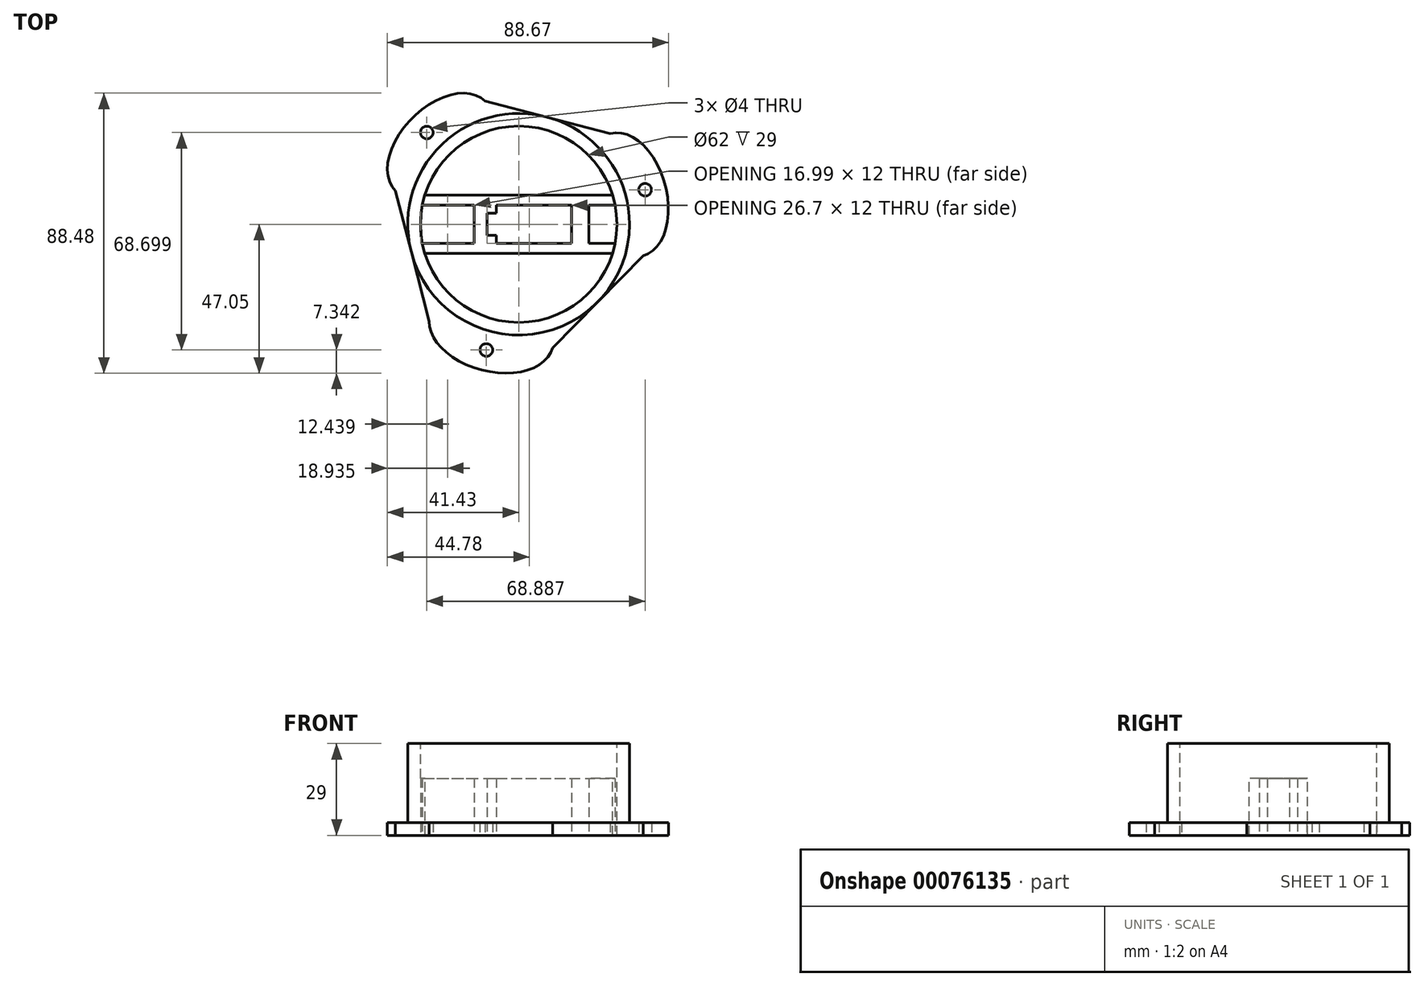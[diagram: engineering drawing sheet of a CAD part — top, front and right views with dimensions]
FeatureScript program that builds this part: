
annotation { "Feature Type Name" : "Feature", "Feature Type Description" : "" }
export const myFeature = defineFeature(function(context is Context, id is Id, definition is map)
    precondition{}
    {
        {
            var Q0;
            Q0=qCreatedBy(makeId("Top.planeOp"),FACE);
            var sketch = newSketch(context, id + "F0", { "sketchPlane" : qUnion([Q0])});
            skCircle(sketch, "E0", {"center": v(0, 0) * mm, "radius": 35 * mm, "construction": true});
            skLineSegment(sketch, "E1", {"start": v(0, 0) * mm, "end": v(-53.68, 53.68) * mm, "construction": true});
            skLineSegment(sketch, "E2", {"start": v(-24.75, 24.75) * mm, "end": v(-10.6, 38.9) * mm, "construction": true});
            skPoint(sketch, "E2.endSnap0", {"position": v(-10.6, 38.9) * mm});
            skPoint(sketch, "E3.center", {"position": v(0.23, 0.06) * mm});
            skLineSegment(sketch, "E4", {"start": v(-10.6, 38.9) * mm, "end": v(28.92, 28.68) * mm});
            skLineSegment(sketch, "E5", {"start": v(39.28, -9.96) * mm, "end": v(10.66, -39.09) * mm});
            skLineSegment(sketch, "E6", {"start": v(-38.9, 10.6) * mm, "end": v(-28.24, -30.6) * mm});
            skLineSegment(sketch, "E7", {"start": v(10.66, -39.09) * mm, "end": v(-8.65, -33.91) * mm, "construction": true});
            skEllipticalArc(sketch, "E8", {});
            skEllipticalArc(sketch, "E9", {"construction": true});
            skEllipticalArc(sketch, "E10", {"construction": true});
            skEllipticalArc(sketch, "E11", {});
            skEllipticalArc(sketch, "E12", {});
            skEllipticalArc(sketch, "E13", {"construction": true});
            skCircle(sketch, "E14", {"center": v(-29, 29) * mm, "radius": 2 * mm});
            skCircle(sketch, "E15.1.0", {"center": v(-10.2, -39.7) * mm, "radius": 2 * mm});
            skCircle(sketch, "E15.2.0", {"center": v(39.9, 10.9) * mm, "radius": 2 * mm});
            const initialGuessF0  = {"E8": [-0.024748737341529166, 0.024748737341529166, 0.7071067811865477, 0.7071067811865475, 0.02, 0.0125, 0, 3.141592653589793], "E9": [-0.024748737341529173, 0.02474873734152916, 0.7071067811865474, 0.7071067811865478, 0.02, 0.0125, 3.141592653589793, 0], "E10": [0.034100125777446366, 0.009356648892922962, 0.258819045102522, -0.965925826289068, 0.02, 0.0125, 3.141592653589793, 0], "E11": [0.034100125777446366, 0.009356648892922962, 0.25881904510252196, -0.965925826289068, 0.02, 0.0125, 0, 3.141592653589793], "E12": [-0.00865424539583139, -0.03391191732763989, -0.9659258262890683, 0.25881904510252074, 0.02, 0.0125, 0.15088942989360254, 3.141592653589793], "E13": [-0.00865424539583139, -0.03391191732763989, -0.9659258262890683, 0.25881904510252074, 0.02, 0.0125, 3.141592653589793, 0.15088942989360254]};
            skSetInitialGuess(sketch, initialGuessF0);
            skSolve(sketch);
        }
        {
            var Q0;
            Q0=makeQuery(id+"F0.imprint","IMPRINT",FACE,{"disambiguationData":[TD([[makeQuery(id+"F0.imprint","IMPRINT",EDGE,{"derivedFrom":sQuery(id+"F0.wireOp",EDGE,"E4")}),-1.0]])]});
            var Q1;
            Q1=sQuery(id+"F0.wireOp",EDGE,"E4");
            var Q2;
            Q2=sQuery(id+"F0.wireOp",EDGE,"E8");
            var Q3;
            Q3=sQuery(id+"F0.wireOp",EDGE,"E6");
            var Q4;
            Q4=sQuery(id+"F0.wireOp",EDGE,"E12");
            var Q5;
            Q5=sQuery(id+"F0.wireOp",EDGE,"E5");
            var Q6;
            Q6=sQuery(id+"F0.wireOp",EDGE,"E11");
            extrude(context, id + "F1", {"entities" : qUnion([Q0]), "surfaceEntities" : qUnion([Q1, Q2, Q3, Q4, Q5, Q6]), "depth" : 4 * mm});
        }
        {
            var Q0;
            Q0=makeQuery(id+"F1.opExtrude","CAP_FACE",FACE,{"disambiguationData":[OSD([sQuery(id+"F0.wireOp",EDGE,"E4"),sQuery(id+"F0.wireOp",EDGE,"E5"),sQuery(id+"F0.wireOp",EDGE,"E6"),sQuery(id+"F0.wireOp",EDGE,"E8"),sQuery(id+"F0.wireOp",EDGE,"E11"),sQuery(id+"F0.wireOp",EDGE,"E12")])],"isStart":false});
            var sketch = newSketch(context, id + "F2", { "sketchPlane" : qUnion([Q0])});
            skCircle(sketch, "E16", {"center": v(0, 0) * mm, "radius": 35 * mm});
            skSolve(sketch);
        }
        {
            var Q0;
            Q0 = qSketchRegion(id + "F2", true);
            extrude(context, id + "F3", {"entities" : qUnion([Q0]), "operationType" : NewBodyOperationType.ADD, "depth" : 25 * mm});
        }
        {
            var Q0;
            Q0=makeQuery(id+"F3.opExtrude","CAP_FACE",FACE,{"disambiguationData":[OSD([sQuery(id+"F2.wireOp",EDGE,"E16")])],"isStart":false});
            var sketch = newSketch(context, id + "F4", { "sketchPlane" : qUnion([Q0])});
            skCircle(sketch, "E17", {"center": v(0, 0) * mm, "radius": 31 * mm});
            skSolve(sketch);
        }
        {
            var Q0;
            Q0=makeQuery(id+"F4.imprint","IMPRINT",FACE,{"disambiguationData":[TD([[makeQuery(id+"F4.imprint","IMPRINT",EDGE,{"derivedFrom":sQuery(id+"F4.wireOp",EDGE,"E17")}),1.0]])]});
            extrude(context, id + "F5", {"entities" : qUnion([Q0]), "operationType" : NewBodyOperationType.REMOVE, "endBound" : BoundingType.THROUGH_ALL, "oppositeDirection" : true, "depth" : 25 * mm});
        }
        {
            var Q0;
            Q0=qCreatedBy(makeId("Top.planeOp"),FACE);
            var sketch = newSketch(context, id + "F6", { "sketchPlane" : qUnion([Q0])});
            skLineSegment(sketch, "E18.bottom", {"start": v(-31.5, 9.25) * mm, "end": v(31.5, 9.25) * mm});
            skLineSegment(sketch, "E18.top", {"start": v(-31.5, -9.25) * mm, "end": v(31.5, -9.25) * mm});
            skLineSegment(sketch, "E18.left", {"start": v(-31.5, 9.25) * mm, "end": v(-31.5, -9.25) * mm});
            skLineSegment(sketch, "E18.right", {"start": v(31.5, 9.25) * mm, "end": v(31.5, -9.25) * mm});
            skPoint(sketch, "E18.middle", {"position": v(0, 0) * mm});
            skSolve(sketch);
        }
        {
            var Q0;
            Q0=makeQuery(id+"F6.imprint","IMPRINT",FACE,{"disambiguationData":[TD([[makeQuery(id+"F6.imprint","IMPRINT",EDGE,{"derivedFrom":sQuery(id+"F6.wireOp",EDGE,"E18.bottom")}),-1.0]])]});
            extrude(context, id + "F7", {"entities" : qUnion([Q0]), "operationType" : NewBodyOperationType.ADD, "depth" : 18 * mm});
        }
        {
            var Q0;
            Q0=qCreatedBy(makeId("Top.planeOp"),FACE);
            var sketch = newSketch(context, id + "F8", { "sketchPlane" : qUnion([Q0])});
            skLineSegment(sketch, "E19.bottom", {"start": v(31.5, 9.25) * mm, "end": v(-31.5, 9.25) * mm});
            skLineSegment(sketch, "E19.top", {"start": v(31.5, -9.25) * mm, "end": v(-31.5, -9.25) * mm});
            skLineSegment(sketch, "E19.left", {"start": v(31.5, 9.25) * mm, "end": v(31.5, -9.25) * mm, "construction": true});
            skLineSegment(sketch, "E19.right", {"start": v(-31.5, 9.25) * mm, "end": v(-31.5, -9.25) * mm, "construction": true});
            skPoint(sketch, "E19.middle", {"position": v(0, 0) * mm});
            skLineSegment(sketch, "E20.bottom", {"start": v(-14, 6) * mm, "end": v(-30.4, 6) * mm});
            skLineSegment(sketch, "E20.top", {"start": v(-14, -6) * mm, "end": v(-32, -6) * mm});
            skLineSegment(sketch, "E20.left", {"start": v(-14, 6) * mm, "end": v(-14, -6) * mm});
            skPoint(sketch, "E20.middle", {"position": v(-23, 0) * mm});
            skLineSegment(sketch, "E21.bottom", {"start": v(16.7, 6) * mm, "end": v(-7, 6) * mm});
            skLineSegment(sketch, "E21.top", {"start": v(16.7, -6) * mm, "end": v(-7, -6) * mm});
            skLineSegment(sketch, "E21.left", {"start": v(16.7, 6) * mm, "end": v(16.7, -6) * mm});
            skLineSegment(sketch, "E21.right", {"start": v(-7, 6) * mm, "end": v(-7, 3.5) * mm});
            skPoint(sketch, "E21.middle", {"position": v(4.85, 0) * mm});
            skLineSegment(sketch, "E22.bottom", {"start": v(-7, 3.5) * mm, "end": v(-10, 3.5) * mm});
            skLineSegment(sketch, "E22.top", {"start": v(-7, -3.5) * mm, "end": v(-10, -3.5) * mm});
            skLineSegment(sketch, "E22.left", {"start": v(-7, 3.5) * mm, "end": v(-7, -3.5) * mm, "construction": true});
            skLineSegment(sketch, "E22.right", {"start": v(-10, 3.5) * mm, "end": v(-10, -3.5) * mm});
            skPoint(sketch, "E22.middle", {"position": v(-8.5, 0) * mm});
            skPoint(sketch, "E22.middle.positionSnap0", {"position": v(-7, 0) * mm});
            skPoint(sketch, "E22.centerSnap0", {"position": v(-7, 0) * mm});
            skLineSegment(sketch, "E23", {"start": v(-7, -3.5) * mm, "end": v(-7, -6) * mm});
            skLineSegment(sketch, "E24.bottom", {"start": v(22.2, 6) * mm, "end": v(30.41, 6) * mm});
            skLineSegment(sketch, "E24.top", {"start": v(22.2, -6) * mm, "end": v(32.33, -6) * mm});
            skLineSegment(sketch, "E24.left", {"start": v(22.2, 6) * mm, "end": v(22.2, -6) * mm});
            skLineSegment(sketch, "E24.right", {"start": v(32.33, 6) * mm, "end": v(32.33, -6) * mm, "construction": true});
            skPoint(sketch, "E24.middle", {"position": v(27.27, 0) * mm});
            skLineSegment(sketch, "E25", {"start": v(30.41, 6) * mm, "end": v(32.33, 6) * mm, "construction": true});
            skArc(sketch, "E26", {"start": v(30.41, -6) * mm, "mid": v(31, 0) * mm, "end": v(30.41, 6) * mm});
            skLineSegment(sketch, "E27", {"start": v(-31.5, 6) * mm, "end": v(-32, 6) * mm});
            skArc(sketch, "E28", {"start": v(-30.41, -6) * mm, "mid": v(-30.04, -7.64) * mm, "end": v(-29.59, -9.25) * mm});
            skArc(sketch, "E29", {"start": v(-30.4, 6) * mm, "mid": v(-31, 0) * mm, "end": v(-30.41, -6) * mm});
            skArc(sketch, "E30.trimOffspring", {"start": v(-29.59, 9.25) * mm, "mid": v(-30.03, 7.64) * mm, "end": v(-30.4, 6) * mm});
            skArc(sketch, "E31.trimOffspring", {"start": v(29.59, -9.25) * mm, "mid": v(30.04, -7.64) * mm, "end": v(30.41, -6) * mm});
            skSolve(sketch);
        }
        {
            var Q0;
            Q0 = qSketchRegion(id + "F8", true);
            extrude(context, id + "F9", {"entities" : qUnion([Q0]), "operationType" : NewBodyOperationType.REMOVE, "endBound" : BoundingType.THROUGH_ALL, "depth" : 25 * mm});
        }
    });
